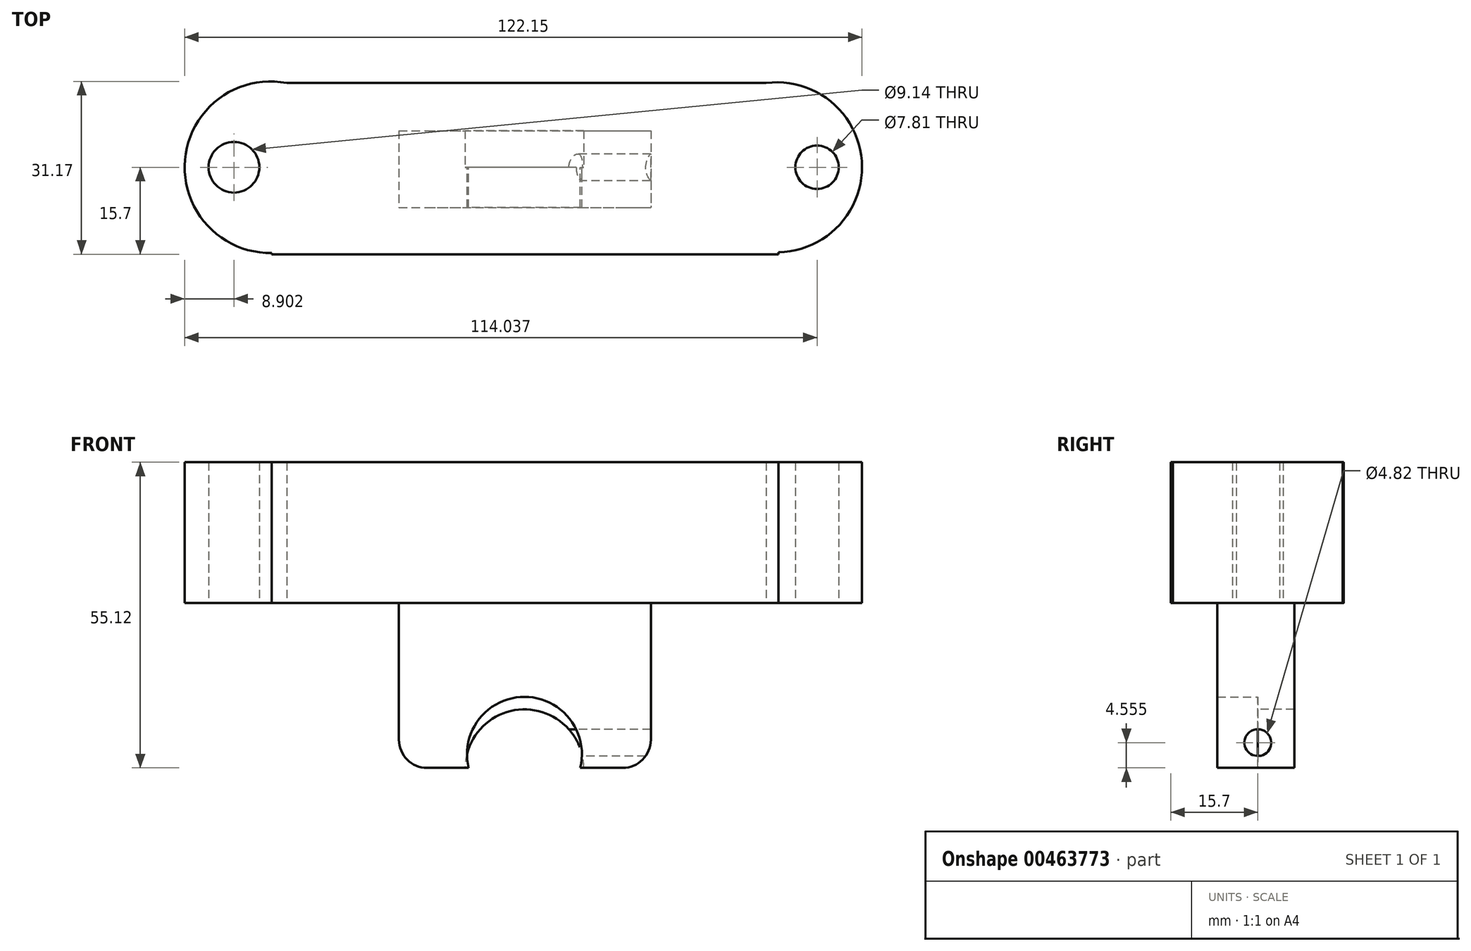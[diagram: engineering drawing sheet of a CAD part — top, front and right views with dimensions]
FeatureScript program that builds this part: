
annotation { "Feature Type Name" : "Feature", "Feature Type Description" : "" }
export const myFeature = defineFeature(function(context is Context, id is Id, definition is map)
    precondition{}
    {
        {
            var Q0;
            Q0=qCreatedBy(makeId("Top.planeOp"),FACE);
            var sketch = newSketch(context, id + "F0", { "sketchPlane" : qUnion([Q0])});
            skLineSegment(sketch, "E0.bottom", {"start": v(-45.56, 15.19) * mm, "end": v(45.81, 15.19) * mm});
            skLineSegment(sketch, "E0.top", {"start": v(-45.56, -15.7) * mm, "end": v(45.81, -15.7) * mm});
            skLineSegment(sketch, "E0.left", {"start": v(-45.56, 15.19) * mm, "end": v(-45.56, -15.7) * mm});
            skLineSegment(sketch, "E0.right", {"start": v(45.81, 15.19) * mm, "end": v(45.81, -15.7) * mm});
            skSolve(sketch);
        }
        {
            var Q0;
            Q0=qCreatedBy(makeId("Top.planeOp"),FACE);
            var sketch = newSketch(context, id + "F1", { "sketchPlane" : qUnion([Q0])});
            skCircle(sketch, "E1", {"center": v(-45.81, 0) * mm, "radius": 15.47 * mm});
            skSolve(sketch);
        }
        {
            var Q0;
            Q0=qCreatedBy(makeId("Top.planeOp"),FACE);
            var sketch = newSketch(context, id + "F2", { "sketchPlane" : qUnion([Q0])});
            skCircle(sketch, "E2", {"center": v(45.56, 0) * mm, "radius": 15.31 * mm});
            skSolve(sketch);
        }
        {
            var Q0;
            Q0=makeQuery(id+"F1.imprint","IMPRINT",FACE,{"disambiguationData":[TD([[makeQuery(id+"F1.imprint","IMPRINT",EDGE,{"derivedFrom":sQuery(id+"F1.wireOp",EDGE,"E1")}),1.0]])]});
            extrude(context, id + "F3", {"entities" : qUnion([Q0]), "depth" : 25.4 * mm});
        }
        {
            var Q0;
            Q0=makeQuery(id+"F0.imprint","IMPRINT",FACE,{"disambiguationData":[TD([[makeQuery(id+"F0.imprint","IMPRINT",EDGE,{"derivedFrom":sQuery(id+"F0.wireOp",EDGE,"E0.bottom")}),-1.0]])]});
            extrude(context, id + "F4", {"entities" : qUnion([Q0]), "operationType" : NewBodyOperationType.ADD, "depth" : 25.4 * mm});
        }
        {
            var Q0;
            Q0=makeQuery(id+"F2.imprint","IMPRINT",FACE,{"disambiguationData":[TD([[makeQuery(id+"F2.imprint","IMPRINT",EDGE,{"derivedFrom":sQuery(id+"F2.wireOp",EDGE,"E2")}),1.0]])]});
            extrude(context, id + "F5", {"entities" : qUnion([Q0]), "operationType" : NewBodyOperationType.ADD, "depth" : 25.4 * mm});
        }
        {
            var Q0;
            Q0=qCreatedBy(makeId("Top.planeOp"),FACE);
            var sketch = newSketch(context, id + "F6", { "sketchPlane" : qUnion([Q0])});
            skCircle(sketch, "E3", {"center": v(-53.03, 0) * mm, "radius": 3.97 * mm});
            skSolve(sketch);
        }
        {
            var Q0;
            Q0=makeQuery(id+"F6.imprint","IMPRINT",FACE,{"disambiguationData":[TD([[makeQuery(id+"F6.imprint","IMPRINT",EDGE,{"derivedFrom":sQuery(id+"F6.wireOp",EDGE,"E3")}),1.0]])]});
            extrude(context, id + "F7", {"entities" : qUnion([Q0]), "operationType" : NewBodyOperationType.REMOVE, "oppositeDirection" : true, "depth" : 25.4 * mm});
        }
        {
            var Q0;
            Q0=qCreatedBy(makeId("Top.planeOp"),FACE);
            var sketch = newSketch(context, id + "F8", { "sketchPlane" : qUnion([Q0])});
            skCircle(sketch, "E4", {"center": v(-52.38, 0) * mm, "radius": 4.57 * mm});
            skSolve(sketch);
        }
        {
            var Q0;
            Q0=makeQuery(id+"F8.imprint","IMPRINT",FACE,{"disambiguationData":[TD([[makeQuery(id+"F8.imprint","IMPRINT",EDGE,{"derivedFrom":sQuery(id+"F8.wireOp",EDGE,"E4")}),1.0]])]});
            extrude(context, id + "F9", {"entities" : qUnion([Q0]), "operationType" : NewBodyOperationType.REMOVE, "depth" : 26.67 * mm});
        }
        {
            var Q0;
            Q0=qCreatedBy(makeId("Top.planeOp"),FACE);
            var sketch = newSketch(context, id + "F10", { "sketchPlane" : qUnion([Q0])});
            skCircle(sketch, "E5", {"center": v(52.76, 0) * mm, "radius": 3.9 * mm});
            skSolve(sketch);
        }
        {
            var Q0;
            Q0=makeQuery(id+"F10.imprint","IMPRINT",FACE,{"disambiguationData":[TD([[makeQuery(id+"F10.imprint","IMPRINT",EDGE,{"derivedFrom":sQuery(id+"F10.wireOp",EDGE,"E5")}),1.0]])]});
            extrude(context, id + "F11", {"entities" : qUnion([Q0]), "operationType" : NewBodyOperationType.REMOVE, "depth" : 30.99 * mm});
        }
        {
            var Q0;
            Q0=qCreatedBy(makeId("Top.planeOp"),FACE);
            var sketch = newSketch(context, id + "F12", { "sketchPlane" : qUnion([Q0])});
            skLineSegment(sketch, "E6.bottom", {"start": v(-22.64, 6.59) * mm, "end": v(22.79, 6.59) * mm});
            skLineSegment(sketch, "E6.top", {"start": v(-22.64, -7.3) * mm, "end": v(22.79, -7.3) * mm});
            skLineSegment(sketch, "E6.left", {"start": v(-22.64, 6.59) * mm, "end": v(-22.64, -7.3) * mm});
            skLineSegment(sketch, "E6.right", {"start": v(22.79, 6.59) * mm, "end": v(22.79, -7.3) * mm});
            skSolve(sketch);
        }
        {
            var Q0;
            Q0=makeQuery(id+"F12.imprint","IMPRINT",FACE,{"disambiguationData":[TD([[makeQuery(id+"F12.imprint","IMPRINT",EDGE,{"derivedFrom":sQuery(id+"F12.wireOp",EDGE,"E6.bottom")}),-1.0]])]});
            extrude(context, id + "F13", {"entities" : qUnion([Q0]), "operationType" : NewBodyOperationType.ADD, "oppositeDirection" : true, "depth" : 29.72 * mm});
        }
        {
            var Q0;
            Q0=qCreatedBy(makeId("Right.planeOp"),FACE);
            var sketch = newSketch(context, id + "F14", { "sketchPlane" : qUnion([Q0])});
            skCircle(sketch, "E7", {"center": v(0, -25.16) * mm, "radius": 2.4 * mm});
            skSolve(sketch);
        }
        {
            var Q0;
            Q0=qCreatedBy(makeId("Front.planeOp"),FACE);
            var sketch = newSketch(context, id + "F15", { "sketchPlane" : qUnion([Q0])});
            skCircle(sketch, "E8", {"center": v(0, -29.87) * mm, "radius": 10.7 * mm});
            skSolve(sketch);
        }
        {
            var Q0;
            Q0=makeQuery(id+"F15.imprint","IMPRINT",FACE,{"disambiguationData":[TD([[makeQuery(id+"F15.imprint","IMPRINT",EDGE,{"derivedFrom":sQuery(id+"F15.wireOp",EDGE,"E8")}),1.0]])]});
            extrude(context, id + "F16", {"entities" : qUnion([Q0]), "operationType" : NewBodyOperationType.REMOVE, "oppositeDirection" : true, "depth" : 25.4 * mm});
        }
        {
            var Q0;
            Q0=qCreatedBy(makeId("Front.planeOp"),FACE);
            var sketch = newSketch(context, id + "F17", { "sketchPlane" : qUnion([Q0])});
            skCircle(sketch, "E9", {"center": v(0, -27.27) * mm, "radius": 10.36 * mm});
            skSolve(sketch);
        }
        {
            var Q0;
            Q0=makeQuery(id+"F17.imprint","IMPRINT",FACE,{"disambiguationData":[TD([[makeQuery(id+"F17.imprint","IMPRINT",EDGE,{"derivedFrom":sQuery(id+"F17.wireOp",EDGE,"E9")}),1.0]])]});
            extrude(context, id + "F18", {"entities" : qUnion([Q0]), "operationType" : NewBodyOperationType.REMOVE, "depth" : 46.74 * mm});
        }
        {
            var Q0;
            Q0=makeQuery(id+"F14.imprint","IMPRINT",FACE,{"disambiguationData":[TD([[makeQuery(id+"F14.imprint","IMPRINT",EDGE,{"derivedFrom":sQuery(id+"F14.wireOp",EDGE,"E7")}),1.0]])]});
            extrude(context, id + "F19", {"entities" : qUnion([Q0]), "operationType" : NewBodyOperationType.REMOVE, "depth" : 44.2 * mm});
        }
        {
            var Q0;
            Q0=makeQuery(id+"F13.opExtrude","CAP_EDGE",EDGE,{"disambiguationData":[OSD([sQuery(id+"F12.wireOp",EDGE,"E6.left")])],"isStart":false});
            fillet(context, id + "F20", {"entities" : qUnion([Q0]), "radius" : 5.08 * mm, "tangentPropagation" : true, "allowEdgeOverflow" : false});
        }
        {
            var Q0;
            Q0=makeQuery(id+"F13.opExtrude","CAP_EDGE",EDGE,{"disambiguationData":[OSD([sQuery(id+"F12.wireOp",EDGE,"E6.right")])],"isStart":false});
            fillet(context, id + "F21", {"entities" : qUnion([Q0]), "radius" : 5.08 * mm, "tangentPropagation" : true, "allowEdgeOverflow" : false});
        }
    });
